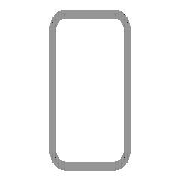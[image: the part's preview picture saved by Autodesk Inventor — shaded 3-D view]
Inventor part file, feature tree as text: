
AUTODESK INVENTOR PART (.ipt)
format: ipt  version: 2025 (Build 290162010, 162A)  size: 133,120 bytes
history: native  units: mm (DEFAULTED — no unit token found)
features: other x4, sketch x1, plane x1
ambient origin geometry x8: Origin, YZ Plane, XZ Plane, XY Plane, X Axis, Y Axis, Z Axis, Center Point
bodies: Solid1 (feature_tree), Body (feature_tree)
feature tree (6):
  parser-record x1  (decoder bookkeeping rows leaked as tree rows — omitted from the tree; the rows remain in map.json)
  other  "Driven Length"
  other  "Start Plane"
  other  "End Plane"
  sketch  "Sketch3"  dims[d3=1380.0mm d4=0.0mm d7=6.0mm d9=40.0mm d11=60.0mm d12=3.0mm d13=60.0mm d14=1440.0mm d15=20.0mm d16=30.0mm d17=90.0deg d18=1380.0mm]
  plane  "Work Plane3"
